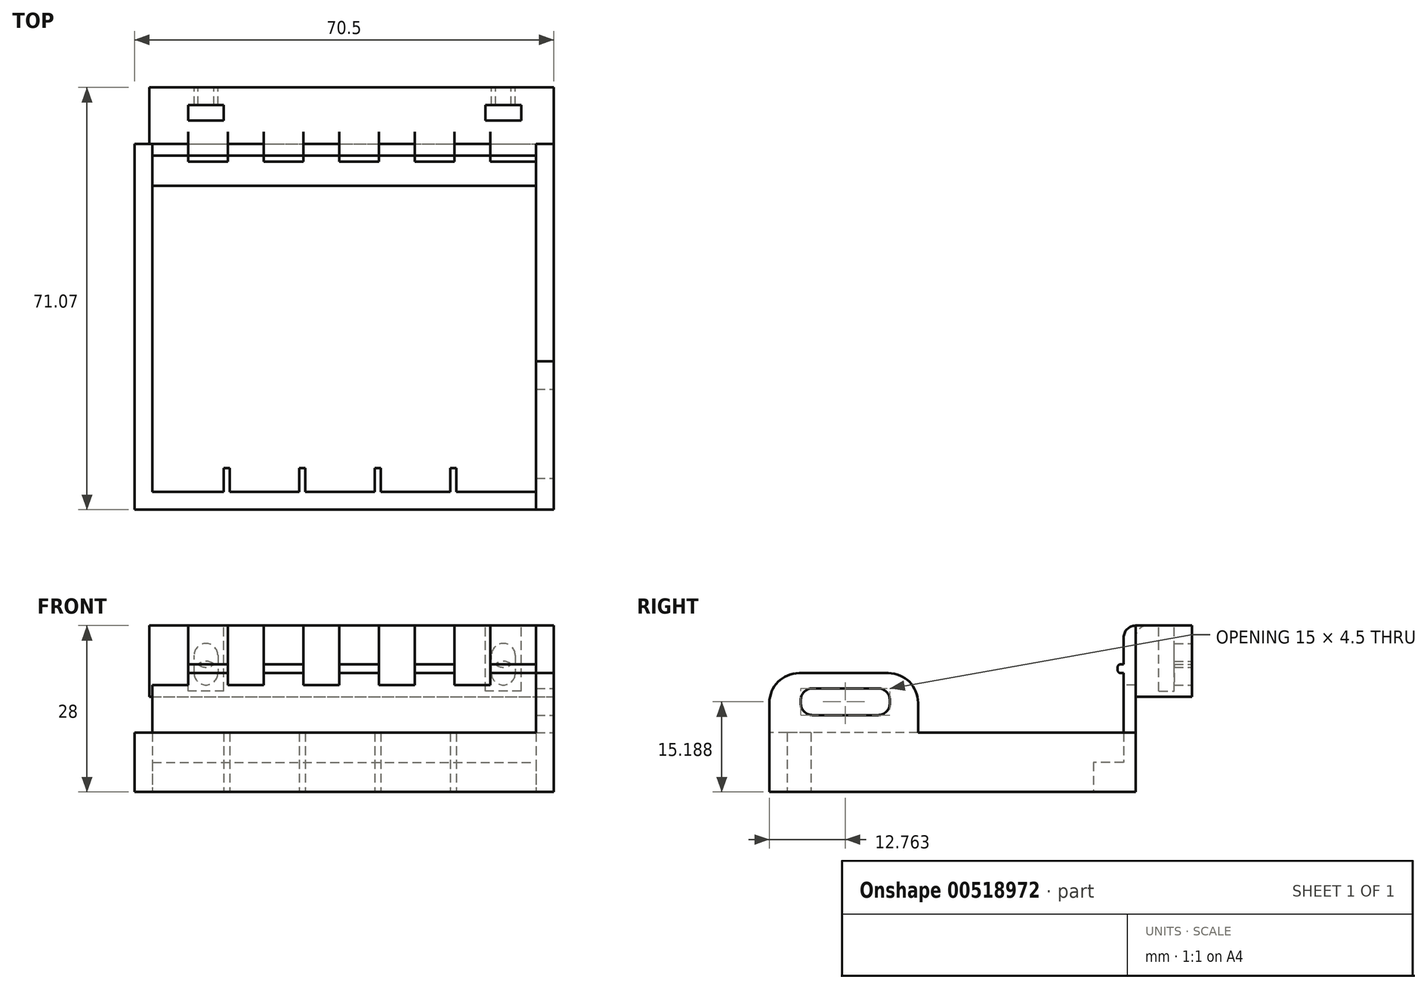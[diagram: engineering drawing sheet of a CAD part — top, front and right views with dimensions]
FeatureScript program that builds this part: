
annotation { "Feature Type Name" : "Feature", "Feature Type Description" : "" }
export const myFeature = defineFeature(function(context is Context, id is Id, definition is map)
    precondition{}
    {
        {
            var Q0;
            Q0=qCreatedBy(makeId("Top.planeOp"),FACE);
            var sketch = newSketch(context, id + "F0", { "sketchPlane" : qUnion([Q0])});
            skLineSegment(sketch, "E0.bottom", {"start": v(-11.89, 33.53) * mm, "end": v(52.61, 33.53) * mm});
            skLineSegment(sketch, "E0.top", {"start": v(-11.89, -23.04) * mm, "end": v(52.61, -23.04) * mm});
            skLineSegment(sketch, "E0.left", {"start": v(-11.89, 33.53) * mm, "end": v(-11.89, -23.04) * mm});
            skLineSegment(sketch, "E0.right", {"start": v(52.61, 33.53) * mm, "end": v(52.61, -23.04) * mm});
            skLineSegment(sketch, "E1.bottom", {"start": v(-14.89, 35.53) * mm, "end": v(55.61, 35.53) * mm});
            skLineSegment(sketch, "E1.top", {"start": v(-14.89, -26.04) * mm, "end": v(55.61, -26.04) * mm});
            skLineSegment(sketch, "E1.left", {"start": v(-14.89, 35.53) * mm, "end": v(-14.89, -26.04) * mm});
            skLineSegment(sketch, "E1.right", {"start": v(55.61, 35.53) * mm, "end": v(55.61, -26.04) * mm});
            skLineSegment(sketch, "E2", {"start": v(-11.89, -5.22) * mm, "end": v(-14.89, -5.22) * mm, "construction": true});
            skLineSegment(sketch, "E3", {"start": v(3.46, -23.04) * mm, "end": v(3.46, -26.04) * mm, "construction": true});
            skLineSegment(sketch, "E4", {"start": v(52.61, -8.08) * mm, "end": v(55.61, -8.08) * mm, "construction": true});
            skLineSegment(sketch, "E5.top", {"start": v(-11.89, 28.46) * mm, "end": v(52.61, 28.46) * mm});
            skLineSegment(sketch, "E5.left", {"start": v(-11.89, 33.53) * mm, "end": v(-11.89, 28.46) * mm});
            skLineSegment(sketch, "E5.right", {"start": v(52.61, 33.53) * mm, "end": v(52.61, 28.46) * mm});
            skLineSegment(sketch, "E6", {"start": v(0.11, -23.04) * mm, "end": v(0.11, -19.04) * mm});
            skLineSegment(sketch, "E7", {"start": v(0.11, -19.04) * mm, "end": v(1.11, -19.04) * mm});
            skLineSegment(sketch, "E8", {"start": v(1.11, -19.04) * mm, "end": v(1.11, -23.04) * mm});
            skLineSegment(sketch, "E9.bottom", {"start": v(12.81, -19.04) * mm, "end": v(13.81, -19.04) * mm});
            skLineSegment(sketch, "E9.top", {"start": v(12.81, -23.04) * mm, "end": v(13.81, -23.04) * mm});
            skLineSegment(sketch, "E9.left", {"start": v(12.81, -19.04) * mm, "end": v(12.81, -23.04) * mm});
            skLineSegment(sketch, "E9.right", {"start": v(13.81, -19.04) * mm, "end": v(13.81, -23.04) * mm});
            skLineSegment(sketch, "E10.bottom", {"start": v(25.51, -19.04) * mm, "end": v(26.51, -19.04) * mm});
            skLineSegment(sketch, "E10.top", {"start": v(25.51, -23.04) * mm, "end": v(26.51, -23.04) * mm});
            skLineSegment(sketch, "E10.left", {"start": v(25.51, -19.04) * mm, "end": v(25.51, -23.04) * mm});
            skLineSegment(sketch, "E10.right", {"start": v(26.51, -19.04) * mm, "end": v(26.51, -23.04) * mm});
            skLineSegment(sketch, "E11.bottom", {"start": v(38.21, -19.04) * mm, "end": v(39.21, -19.04) * mm});
            skLineSegment(sketch, "E11.top", {"start": v(38.21, -23.04) * mm, "end": v(39.21, -23.04) * mm});
            skLineSegment(sketch, "E11.left", {"start": v(38.21, -19.04) * mm, "end": v(38.21, -23.04) * mm});
            skLineSegment(sketch, "E11.right", {"start": v(39.21, -19.04) * mm, "end": v(39.21, -23.04) * mm});
            skSolve(sketch);
        }
        {
            var Q0;
            Q0=makeQuery(id+"F0.imprint","IMPRINT",FACE,{"disambiguationData":[TD([[makeQuery(id+"F0.imprint","IMPRINT",EDGE,{"derivedFrom":sQuery(id+"F0.wireOp",EDGE,"E0.top")}),-1.0]])]});
            var Q1;
            {var subQ0=sQuery(id+"F0.wireOp",EDGE,"E6");Q1=makeQuery(id+"F0.imprint","IMPRINT",FACE,{"disambiguationData":[TD([[makeQuery(id+"F0.imprint","IMPRINT",EDGE,{"derivedFrom":subQ0}),-1.0]])]});}
            var Q2;
            Q2=makeQuery(id+"F0.imprint","IMPRINT",FACE,{"disambiguationData":[TD([[makeQuery(id+"F0.imprint","IMPRINT",EDGE,{"derivedFrom":sQuery(id+"F0.wireOp",EDGE,"E9.bottom")}),-1.0]])]});
            var Q3;
            Q3=makeQuery(id+"F0.imprint","IMPRINT",FACE,{"disambiguationData":[TD([[makeQuery(id+"F0.imprint","IMPRINT",EDGE,{"derivedFrom":sQuery(id+"F0.wireOp",EDGE,"E10.bottom")}),-1.0]])]});
            var Q4;
            Q4=makeQuery(id+"F0.imprint","IMPRINT",FACE,{"disambiguationData":[TD([[makeQuery(id+"F0.imprint","IMPRINT",EDGE,{"derivedFrom":sQuery(id+"F0.wireOp",EDGE,"E11.bottom")}),-1.0]])]});
            extrude(context, id + "F1", {"entities" : qUnion([Q0, Q1, Q2, Q3, Q4]), "depth" : 10 * mm, "offsetDistance" : 25 * mm});
        }
        {
            var Q0;
            Q0=makeQuery(id+"F0.imprint","IMPRINT",FACE,{"disambiguationData":[TD([[makeQuery(id+"F0.imprint","IMPRINT",EDGE,{"derivedFrom":sQuery(id+"F0.wireOp",EDGE,"E0.bottom")}),-1.0]])]});
            extrude(context, id + "F2", {"entities" : qUnion([Q0]), "operationType" : NewBodyOperationType.ADD, "depth" : 5 * mm, "offsetDistance" : 25 * mm});
        }
        {
            var Q0;
            Q0=makeQuery(id+"F1.opExtrude","CAP_FACE",FACE,{"disambiguationData":[OSD([sQuery(id+"F0.wireOp",EDGE,"E0.top"),sQuery(id+"F0.wireOp",EDGE,"E0.left"),sQuery(id+"F0.wireOp",EDGE,"E0.right"),sQuery(id+"F0.wireOp",EDGE,"E1.bottom"),sQuery(id+"F0.wireOp",EDGE,"E1.top"),sQuery(id+"F0.wireOp",EDGE,"E1.left"),sQuery(id+"F0.wireOp",EDGE,"E1.right"),sQuery(id+"F0.wireOp",EDGE,"E0.bottom"),sQuery(id+"F0.wireOp",EDGE,"E5.left"),sQuery(id+"F0.wireOp",EDGE,"E5.right"),sQuery(id+"F0.wireOp",EDGE,"E6"),sQuery(id+"F0.wireOp",EDGE,"E7"),sQuery(id+"F0.wireOp",EDGE,"E8")])],"isStart":false});
            var sketch = newSketch(context, id + "F3", { "sketchPlane" : qUnion([Q0])});
            skLineSegment(sketch, "E12.bottom", {"start": v(-11.89, 33.53) * mm, "end": v(52.61, 33.53) * mm});
            skLineSegment(sketch, "E12.top", {"start": v(-11.89, 35.53) * mm, "end": v(52.61, 35.53) * mm});
            skLineSegment(sketch, "E12.left", {"start": v(-11.89, 33.53) * mm, "end": v(-11.89, 35.53) * mm});
            skLineSegment(sketch, "E12.right", {"start": v(52.61, 33.53) * mm, "end": v(52.61, 35.53) * mm});
            skSolve(sketch);
        }
        {
            var Q0;
            Q0=makeQuery(id+"F3.imprint","IMPRINT",FACE,{"disambiguationData":[TD([[makeQuery(id+"F3.imprint","IMPRINT",EDGE,{"derivedFrom":sQuery(id+"F3.wireOp",EDGE,"E12.bottom")}),1.0]])]});
            extrude(context, id + "F4", {"entities" : qUnion([Q0]), "operationType" : NewBodyOperationType.ADD, "depth" : 18 * mm, "offsetDistance" : 25 * mm});
        }
        {
            var Q0;
            Q0=makeQuery(id+"F4.opExtrude","SWEPT_FACE",FACE,{"disambiguationData":[OSD([sQuery(id+"F3.wireOp",EDGE,"E12.right")])]});
            var sketch = newSketch(context, id + "F5", { "sketchPlane" : qUnion([Q0])});
            skLineSegment(sketch, "E13.bottom", {"start": v(33.53, 21.5) * mm, "end": v(32.53, 21.5) * mm});
            skLineSegment(sketch, "E13.top", {"start": v(33.53, 20) * mm, "end": v(32.53, 20) * mm});
            skLineSegment(sketch, "E13.left", {"start": v(33.53, 21.5) * mm, "end": v(33.53, 20) * mm});
            skLineSegment(sketch, "E13.right", {"start": v(32.53, 21.5) * mm, "end": v(32.53, 20) * mm});
            skSolve(sketch);
        }
        {
            var Q0;
            Q0=makeQuery(id+"F5.imprint","IMPRINT",FACE,{"disambiguationData":[TD([[makeQuery(id+"F5.imprint","IMPRINT",EDGE,{"derivedFrom":sQuery(id+"F5.wireOp",EDGE,"E13.bottom")}),1.0]])]});
            extrude(context, id + "F6", {"entities" : qUnion([Q0]), "operationType" : NewBodyOperationType.ADD, "oppositeDirection" : true, "depth" : 64.5 * mm, "offsetDistance" : 25 * mm});
        }
        {
            var Q0;
            Q0=makeQuery(id+"F6.opExtrude","SWEPT_EDGE",EDGE,{"disambiguationData":[OSD([sQuery(id+"F5.wireOp",EDGE,"E13.bottom"),sQuery(id+"F5.wireOp",EDGE,"E13.right")])]});
            var Q1;
            Q1=makeQuery(id+"F6.opExtrude","SWEPT_EDGE",EDGE,{"disambiguationData":[OSD([sQuery(id+"F5.wireOp",EDGE,"E13.top"),sQuery(id+"F5.wireOp",EDGE,"E13.right")])]});
            fillet(context, id + "F7", {"entities" : qUnion([Q0, Q1]), "radius" : 0.5 * mm, "tangentPropagation" : true, "allowEdgeOverflow" : false});
        }
        {
            var Q0;
            Q0=makeQuery(id+"F4.opExtrude","CAP_FACE",FACE,{"disambiguationData":[OSD([sQuery(id+"F3.wireOp",EDGE,"E12.bottom"),sQuery(id+"F3.wireOp",EDGE,"E12.top"),sQuery(id+"F3.wireOp",EDGE,"E12.left"),sQuery(id+"F3.wireOp",EDGE,"E12.right")])],"isStart":false});
            var sketch = newSketch(context, id + "F8", { "sketchPlane" : qUnion([Q0])});
            skLineSegment(sketch, "E14.bottom", {"start": v(-11.89, 35.53) * mm, "end": v(-5.89, 35.53) * mm});
            skLineSegment(sketch, "E14.top", {"start": v(-11.89, 26.38) * mm, "end": v(-5.89, 26.38) * mm});
            skLineSegment(sketch, "E14.left", {"start": v(-11.89, 35.53) * mm, "end": v(-11.89, 26.38) * mm});
            skLineSegment(sketch, "E14.right", {"start": v(-5.89, 35.53) * mm, "end": v(-5.89, 26.38) * mm});
            skLineSegment(sketch, "E15.bottom", {"start": v(0.81, 35.53) * mm, "end": v(6.81, 35.53) * mm});
            skLineSegment(sketch, "E15.top", {"start": v(0.81, 26.38) * mm, "end": v(6.81, 26.38) * mm});
            skLineSegment(sketch, "E15.left", {"start": v(0.81, 35.53) * mm, "end": v(0.81, 26.38) * mm});
            skLineSegment(sketch, "E15.right", {"start": v(6.81, 35.53) * mm, "end": v(6.81, 26.38) * mm});
            skLineSegment(sketch, "E16.bottom", {"start": v(13.51, 35.53) * mm, "end": v(19.51, 35.53) * mm});
            skLineSegment(sketch, "E16.top", {"start": v(13.51, 26.38) * mm, "end": v(19.51, 26.38) * mm});
            skLineSegment(sketch, "E16.left", {"start": v(13.51, 35.53) * mm, "end": v(13.51, 26.38) * mm});
            skLineSegment(sketch, "E16.right", {"start": v(19.51, 35.53) * mm, "end": v(19.51, 26.38) * mm});
            skLineSegment(sketch, "E17.bottom", {"start": v(26.21, 35.53) * mm, "end": v(32.21, 35.53) * mm});
            skLineSegment(sketch, "E17.top", {"start": v(26.21, 26.38) * mm, "end": v(32.21, 26.38) * mm});
            skLineSegment(sketch, "E17.left", {"start": v(26.21, 35.53) * mm, "end": v(26.21, 26.38) * mm});
            skLineSegment(sketch, "E17.right", {"start": v(32.21, 35.53) * mm, "end": v(32.21, 26.38) * mm});
            skLineSegment(sketch, "E18.bottom", {"start": v(38.91, 35.53) * mm, "end": v(44.91, 35.53) * mm});
            skLineSegment(sketch, "E18.top", {"start": v(38.91, 26.38) * mm, "end": v(44.91, 26.38) * mm});
            skLineSegment(sketch, "E18.left", {"start": v(38.91, 35.53) * mm, "end": v(38.91, 26.38) * mm});
            skLineSegment(sketch, "E18.right", {"start": v(44.91, 35.53) * mm, "end": v(44.91, 26.38) * mm});
            skLineSegment(sketch, "E19", {"start": v(-11.89, 30.96) * mm, "end": v(0.81, 30.96) * mm, "construction": true});
            skLineSegment(sketch, "E20", {"start": v(0.81, 30.96) * mm, "end": v(13.51, 30.96) * mm, "construction": true});
            skLineSegment(sketch, "E21", {"start": v(13.51, 30.96) * mm, "end": v(26.21, 30.96) * mm, "construction": true});
            skLineSegment(sketch, "E22", {"start": v(26.21, 30.96) * mm, "end": v(38.91, 30.96) * mm, "construction": true});
            skSolve(sketch);
        }
        {
            var Q0;
            Q0=qSketchRegion(id+"F8",true);
            extrude(context, id + "F9", {"entities" : qUnion([Q0]), "operationType" : NewBodyOperationType.REMOVE, "oppositeDirection" : true, "depth" : 10 * mm, "offsetDistance" : 25 * mm});
        }
        {
            var Q0;
            Q0=makeQuery(id+"F1.opExtrude","SWEPT_FACE",FACE,{"disambiguationData":[OSD([sQuery(id+"F0.wireOp",EDGE,"E1.right")])]});
            var sketch = newSketch(context, id + "F10", { "sketchPlane" : qUnion([Q0])});
            skLineSegment(sketch, "E23.bottom", {"start": v(35.53, 28) * mm, "end": v(45.03, 28) * mm});
            skLineSegment(sketch, "E23.top", {"start": v(35.53, 16) * mm, "end": v(45.03, 16) * mm});
            skLineSegment(sketch, "E23.left", {"start": v(35.53, 28) * mm, "end": v(35.53, 16) * mm});
            skLineSegment(sketch, "E23.right", {"start": v(45.03, 28) * mm, "end": v(45.03, 16) * mm});
            skSolve(sketch);
        }
        {
            var Q0;
            Q0=makeQuery(id+"F10.imprint","IMPRINT",FACE,{"disambiguationData":[TD([[makeQuery(id+"F10.imprint","IMPRINT",EDGE,{"derivedFrom":sQuery(id+"F10.wireOp",EDGE,"E23.bottom")}),-1.0]])]});
            extrude(context, id + "F11", {"entities" : qUnion([Q0]), "operationType" : NewBodyOperationType.ADD, "oppositeDirection" : true, "depth" : 68 * mm, "offsetDistance" : 25 * mm});
        }
        {
            var Q0;
            Q0=makeQuery(id+"F11.opExtrude","SWEPT_FACE",FACE,{"disambiguationData":[OSD([sQuery(id+"F10.wireOp",EDGE,"E23.right")])]});
            var sketch = newSketch(context, id + "F12", { "sketchPlane" : qUnion([Q0])});
            skCircle(sketch, "E24", {"center": v(-47.11, 20) * mm, "radius": 2 * mm});
            skCircle(sketch, "E25", {"center": v(2.89, 20) * mm, "radius": 2 * mm});
            skCircle(sketch, "E26", {"center": v(-47.11, 23) * mm, "radius": 2 * mm});
            skCircle(sketch, "E27", {"center": v(2.89, 23) * mm, "radius": 2 * mm});
            skLineSegment(sketch, "E28", {"start": v(2.89, 23) * mm, "end": v(0.89, 23) * mm, "construction": true});
            skLineSegment(sketch, "E29", {"start": v(0.89, 23) * mm, "end": v(0.89, 20) * mm});
            skLineSegment(sketch, "E30", {"start": v(0.89, 20) * mm, "end": v(4.89, 20) * mm, "construction": true});
            skLineSegment(sketch, "E31", {"start": v(4.89, 20) * mm, "end": v(4.89, 23) * mm});
            skLineSegment(sketch, "E32", {"start": v(-47.11, 23) * mm, "end": v(-49.11, 23) * mm, "construction": true});
            skLineSegment(sketch, "E33", {"start": v(-49.11, 23) * mm, "end": v(-49.11, 20) * mm});
            skLineSegment(sketch, "E34", {"start": v(-49.11, 20) * mm, "end": v(-45.11, 20) * mm, "construction": true});
            skLineSegment(sketch, "E35", {"start": v(-45.11, 20) * mm, "end": v(-45.11, 23) * mm});
            skSolve(sketch);
        }
        {
            var Q0;
            Q0 = qSketchRegion(id + "F12", true);
            var Q1;
            {var subQ0=sQuery(id+"F12.wireOp",EDGE,"E26");var subQ1=sQuery(id+"F12.wireOp",EDGE,"E24");var subQ2=makeQuery(id+"F12.imprint","INTERSECT",VERTEX,{"disambiguationData":[OD(0.0)],"derivedFrom":[subQ1,subQ0]});Q1=makeQuery(id+"F12.imprint","IMPRINT",FACE,{"disambiguationData":[TD([[makeQuery(id+"F12.imprint","IMPRINT",EDGE,{"disambiguationData":[TD([[subQ2,-1.0]])],"derivedFrom":subQ1}),1.0]])]});}
            var Q2;
            {var subQ0=sQuery(id+"F12.wireOp",EDGE,"E27");var subQ1=sQuery(id+"F12.wireOp",EDGE,"E25");var subQ2=makeQuery(id+"F12.imprint","INTERSECT",VERTEX,{"disambiguationData":[OD(0.0)],"derivedFrom":[subQ1,subQ0]});Q2=makeQuery(id+"F12.imprint","IMPRINT",FACE,{"disambiguationData":[TD([[makeQuery(id+"F12.imprint","IMPRINT",EDGE,{"disambiguationData":[TD([[subQ2,-1.0]])],"derivedFrom":subQ1}),1.0]])]});}
            extrude(context, id + "F13", {"entities" : qUnion([Q0, Q1, Q2]), "operationType" : NewBodyOperationType.REMOVE, "oppositeDirection" : true, "depth" : 4 * mm, "offsetDistance" : 25 * mm});
        }
        {
            var Q0;
            {var subQ0=sQuery(id+"F3.wireOp",EDGE,"E12.bottom");var subQ3=sQuery(id+"F3.wireOp",EDGE,"E12.top");var subQ6=sQuery(id+"F3.wireOp",EDGE,"E12.right");var subQ7=makeQuery(id+"F4.opExtrude","CAP_FACE",FACE,{"disambiguationData":[OSD([subQ0,subQ3,sQuery(id+"F3.wireOp",EDGE,"E12.left"),subQ6])],"isStart":false});Q0=makeQuery(id+"F11.boolean.opBoolean","MERGE",FACE,{"derivedFrom":[makeQuery(id+"F9.boolean.opBoolean","SPLIT",FACE,{"disambiguationData":[TD([makeQuery(id+"F4.opExtrude","SWEPT_FACE",FACE,{"disambiguationData":[OSD([subQ6])]})])],"derivedFrom":subQ7}),makeQuery(id+"F9.boolean.opBoolean","SPLIT",FACE,{"disambiguationData":[TD([makeQuery(id+"F9.opExtrude","SWEPT_FACE",FACE,{"disambiguationData":[OSD([sQuery(id+"F8.wireOp",EDGE,"E14.right")])]})])],"derivedFrom":subQ7}),makeQuery(id+"F9.boolean.opBoolean","SPLIT",FACE,{"disambiguationData":[TD([makeQuery(id+"F9.opExtrude","SWEPT_FACE",FACE,{"disambiguationData":[OSD([sQuery(id+"F8.wireOp",EDGE,"E15.right")])]})])],"derivedFrom":subQ7}),makeQuery(id+"F9.boolean.opBoolean","SPLIT",FACE,{"disambiguationData":[TD([makeQuery(id+"F9.opExtrude","SWEPT_FACE",FACE,{"disambiguationData":[OSD([sQuery(id+"F8.wireOp",EDGE,"E16.right")])]})])],"derivedFrom":subQ7}),makeQuery(id+"F9.boolean.opBoolean","SPLIT",FACE,{"disambiguationData":[TD([makeQuery(id+"F9.opExtrude","SWEPT_FACE",FACE,{"disambiguationData":[OSD([sQuery(id+"F8.wireOp",EDGE,"E17.right")])]})])],"derivedFrom":subQ7}),makeQuery(id+"F11.opExtrude","SWEPT_FACE",FACE,{"disambiguationData":[OSD([sQuery(id+"F10.wireOp",EDGE,"E23.bottom")])]})]});}
            var sketch = newSketch(context, id + "F14", { "sketchPlane" : qUnion([Q0])});
            skLineSegment(sketch, "E36.bottom", {"start": v(0.11, 39.43) * mm, "end": v(-5.89, 39.43) * mm});
            skLineSegment(sketch, "E36.top", {"start": v(0.11, 42.03) * mm, "end": v(-5.89, 42.03) * mm});
            skLineSegment(sketch, "E36.left", {"start": v(0.11, 39.43) * mm, "end": v(0.11, 42.03) * mm});
            skLineSegment(sketch, "E36.right", {"start": v(-5.89, 39.43) * mm, "end": v(-5.89, 42.03) * mm});
            skPoint(sketch, "E36.middle", {"position": v(-2.89, 40.73) * mm});
            skLineSegment(sketch, "E37.bottom", {"start": v(50.11, 39.43) * mm, "end": v(44.11, 39.43) * mm});
            skLineSegment(sketch, "E37.top", {"start": v(50.11, 42.03) * mm, "end": v(44.11, 42.03) * mm});
            skLineSegment(sketch, "E37.left", {"start": v(50.11, 39.43) * mm, "end": v(50.11, 42.03) * mm});
            skLineSegment(sketch, "E37.right", {"start": v(44.11, 39.43) * mm, "end": v(44.11, 42.03) * mm});
            skPoint(sketch, "E37.middle", {"position": v(47.11, 40.73) * mm});
            skSolve(sketch);
        }
        {
            var Q0;
            Q0 = qSketchRegion(id + "F14", true);
            extrude(context, id + "F15", {"entities" : qUnion([Q0]), "operationType" : NewBodyOperationType.REMOVE, "oppositeDirection" : true, "depth" : 11 * mm, "offsetDistance" : 25 * mm});
        }
        {
            var Q0;
            Q0=makeQuery(id+"F1.opExtrude","CAP_FACE",FACE,{"disambiguationData":[OSD([sQuery(id+"F0.wireOp",EDGE,"E0.top"),sQuery(id+"F0.wireOp",EDGE,"E0.left"),sQuery(id+"F0.wireOp",EDGE,"E0.right"),sQuery(id+"F0.wireOp",EDGE,"E1.bottom"),sQuery(id+"F0.wireOp",EDGE,"E1.top"),sQuery(id+"F0.wireOp",EDGE,"E1.left"),sQuery(id+"F0.wireOp",EDGE,"E1.right"),sQuery(id+"F0.wireOp",EDGE,"E0.bottom"),sQuery(id+"F0.wireOp",EDGE,"E5.left"),sQuery(id+"F0.wireOp",EDGE,"E5.right"),sQuery(id+"F0.wireOp",EDGE,"E6"),sQuery(id+"F0.wireOp",EDGE,"E7"),sQuery(id+"F0.wireOp",EDGE,"E8"),sQuery(id+"F0.wireOp",EDGE,"E9.bottom"),sQuery(id+"F0.wireOp",EDGE,"E9.left"),sQuery(id+"F0.wireOp",EDGE,"E9.right"),sQuery(id+"F0.wireOp",EDGE,"E10.bottom"),sQuery(id+"F0.wireOp",EDGE,"E10.left"),sQuery(id+"F0.wireOp",EDGE,"E10.right"),sQuery(id+"F0.wireOp",EDGE,"E11.bottom"),sQuery(id+"F0.wireOp",EDGE,"E11.left"),sQuery(id+"F0.wireOp",EDGE,"E11.right")])],"isStart":false});
            var sketch = newSketch(context, id + "F16", { "sketchPlane" : qUnion([Q0])});
            skLineSegment(sketch, "E38.bottom", {"start": v(55.61, -26.04) * mm, "end": v(52.61, -26.04) * mm});
            skLineSegment(sketch, "E38.top", {"start": v(55.61, -1.04) * mm, "end": v(52.61, -1.04) * mm});
            skLineSegment(sketch, "E38.left", {"start": v(55.61, -26.04) * mm, "end": v(55.61, -1.04) * mm});
            skLineSegment(sketch, "E38.right", {"start": v(52.61, -26.04) * mm, "end": v(52.61, -1.04) * mm});
            skSolve(sketch);
        }
        {
            var Q0;
            {var subQ4=sQuery(id+"F16.wireOp",EDGE,"E38.bottom");Q0=makeQuery(id+"F16.imprint","IMPRINT",FACE,{"disambiguationData":[TD([[makeQuery(id+"F16.imprint","IMPRINT",EDGE,{"derivedFrom":subQ4}),1.0]])]});}
            extrude(context, id + "F17", {"entities" : qUnion([Q0]), "operationType" : NewBodyOperationType.ADD, "depth" : 10 * mm, "offsetDistance" : 25 * mm});
        }
        {
            var Q0;
            Q0=makeQuery(id+"F17.boolean.opBoolean","MERGE",FACE,{"derivedFrom":[makeQuery(id+"F1.opExtrude","SWEPT_FACE",FACE,{"disambiguationData":[OSD([sQuery(id+"F0.wireOp",EDGE,"E1.right")])]}),makeQuery(id+"F17.opExtrude","SWEPT_FACE",FACE,{"disambiguationData":[OSD([sQuery(id+"F16.wireOp",EDGE,"E38.left")])]})]});
            var sketch = newSketch(context, id + "F18", { "sketchPlane" : qUnion([Q0])});
            skLineSegment(sketch, "E39.bottom", {"start": v(-20.78, 17.44) * mm, "end": v(-5.78, 17.44) * mm});
            skLineSegment(sketch, "E39.top", {"start": v(-20.78, 12.94) * mm, "end": v(-5.78, 12.94) * mm});
            skLineSegment(sketch, "E39.left", {"start": v(-20.78, 17.44) * mm, "end": v(-20.78, 12.94) * mm});
            skLineSegment(sketch, "E39.right", {"start": v(-5.78, 17.44) * mm, "end": v(-5.78, 12.94) * mm});
            skSolve(sketch);
        }
        {
            var Q0;
            Q0=makeQuery(id+"F18.imprint","IMPRINT",FACE,{"disambiguationData":[TD([[makeQuery(id+"F18.imprint","IMPRINT",EDGE,{"derivedFrom":sQuery(id+"F18.wireOp",EDGE,"E39.bottom")}),-1.0]])]});
            extrude(context, id + "F19", {"entities" : qUnion([Q0]), "operationType" : NewBodyOperationType.REMOVE, "oppositeDirection" : true, "depth" : 25 * mm, "offsetDistance" : 25 * mm});
        }
        {
            var Q0;
            Q0=makeQuery(id+"F17.opExtrude","CAP_EDGE",EDGE,{"disambiguationData":[OSD([sQuery(id+"F16.wireOp",EDGE,"E38.top")])],"isStart":false});
            var Q1;
            Q1=makeQuery(id+"F17.opExtrude","CAP_EDGE",EDGE,{"disambiguationData":[OSD([sQuery(id+"F16.wireOp",EDGE,"E38.bottom")])],"isStart":false});
            fillet(context, id + "F20", {"entities" : qUnion([Q0, Q1]), "radius" : 5 * mm, "tangentPropagation" : true, "allowEdgeOverflow" : false});
        }
        {
            var Q0;
            Q0=makeQuery(id+"F19.boolean.opBoolean","COPY",EDGE,{"derivedFrom":makeQuery(id+"F19.opExtrude","SWEPT_EDGE",EDGE,{"disambiguationData":[OSD([sQuery(id+"F18.wireOp",EDGE,"E39.bottom"),sQuery(id+"F18.wireOp",EDGE,"E39.left")])]})});
            var Q1;
            Q1=makeQuery(id+"F19.boolean.opBoolean","COPY",EDGE,{"derivedFrom":makeQuery(id+"F19.opExtrude","SWEPT_EDGE",EDGE,{"disambiguationData":[OSD([sQuery(id+"F18.wireOp",EDGE,"E39.top"),sQuery(id+"F18.wireOp",EDGE,"E39.left")])]})});
            var Q2;
            Q2=makeQuery(id+"F19.boolean.opBoolean","COPY",EDGE,{"derivedFrom":makeQuery(id+"F19.opExtrude","SWEPT_EDGE",EDGE,{"disambiguationData":[OSD([sQuery(id+"F18.wireOp",EDGE,"E39.top"),sQuery(id+"F18.wireOp",EDGE,"E39.right")])]})});
            var Q3;
            Q3=makeQuery(id+"F19.boolean.opBoolean","COPY",EDGE,{"derivedFrom":makeQuery(id+"F19.opExtrude","SWEPT_EDGE",EDGE,{"disambiguationData":[OSD([sQuery(id+"F18.wireOp",EDGE,"E39.bottom"),sQuery(id+"F18.wireOp",EDGE,"E39.right")])]})});
            var Q4;
            {var subQ0=sQuery(id+"F10.wireOp",EDGE,"E23.bottom");var subQ1=sQuery(id+"F10.wireOp",EDGE,"E23.left");Q4=makeQuery(id+"F11.boolean.opBoolean","SPLIT",EDGE,{"disambiguationData":[TD([makeQuery(id+"F9.boolean.opBoolean","COPY",FACE,{"derivedFrom":makeQuery(id+"F9.opExtrude","SWEPT_FACE",FACE,{"disambiguationData":[OSD([sQuery(id+"F8.wireOp",EDGE,"E18.left")])]})})])],"derivedFrom":makeQuery(id+"F11.opExtrude","SWEPT_EDGE",EDGE,{"disambiguationData":[OSD([subQ0,subQ1])]})});}
            var Q5;
            {var subQ0=sQuery(id+"F3.wireOp",EDGE,"E12.right");var subQ1=sQuery(id+"F3.wireOp",EDGE,"E12.bottom");Q5=makeQuery(id+"F9.boolean.opBoolean","SPLIT",EDGE,{"disambiguationData":[TD([makeQuery(id+"F4.opExtrude","SWEPT_FACE",FACE,{"disambiguationData":[OSD([subQ0])]})])],"derivedFrom":makeQuery(id+"F4.opExtrude","CAP_EDGE",EDGE,{"disambiguationData":[OSD([subQ1])],"isStart":false})});}
            var Q6;
            {var subQ0=sQuery(id+"F3.wireOp",EDGE,"E12.bottom");Q6=makeQuery(id+"F9.boolean.opBoolean","SPLIT",EDGE,{"disambiguationData":[TD([makeQuery(id+"F9.opExtrude","SWEPT_FACE",FACE,{"disambiguationData":[OSD([sQuery(id+"F8.wireOp",EDGE,"E17.right")])]})])],"derivedFrom":makeQuery(id+"F4.opExtrude","CAP_EDGE",EDGE,{"disambiguationData":[OSD([subQ0])],"isStart":false})});}
            var Q7;
            {var subQ0=sQuery(id+"F10.wireOp",EDGE,"E23.bottom");var subQ1=sQuery(id+"F10.wireOp",EDGE,"E23.left");Q7=makeQuery(id+"F11.boolean.opBoolean","SPLIT",EDGE,{"disambiguationData":[TD([makeQuery(id+"F9.boolean.opBoolean","COPY",FACE,{"derivedFrom":makeQuery(id+"F9.opExtrude","SWEPT_FACE",FACE,{"disambiguationData":[OSD([sQuery(id+"F8.wireOp",EDGE,"E17.left")])]})})])],"derivedFrom":makeQuery(id+"F11.opExtrude","SWEPT_EDGE",EDGE,{"disambiguationData":[OSD([subQ0,subQ1])]})});}
            var Q8;
            {var subQ0=sQuery(id+"F3.wireOp",EDGE,"E12.bottom");Q8=makeQuery(id+"F9.boolean.opBoolean","SPLIT",EDGE,{"disambiguationData":[TD([makeQuery(id+"F9.opExtrude","SWEPT_FACE",FACE,{"disambiguationData":[OSD([sQuery(id+"F8.wireOp",EDGE,"E16.right")])]})])],"derivedFrom":makeQuery(id+"F4.opExtrude","CAP_EDGE",EDGE,{"disambiguationData":[OSD([subQ0])],"isStart":false})});}
            var Q9;
            {var subQ0=sQuery(id+"F10.wireOp",EDGE,"E23.bottom");var subQ1=sQuery(id+"F10.wireOp",EDGE,"E23.left");Q9=makeQuery(id+"F11.boolean.opBoolean","SPLIT",EDGE,{"disambiguationData":[TD([makeQuery(id+"F9.boolean.opBoolean","COPY",FACE,{"derivedFrom":makeQuery(id+"F9.opExtrude","SWEPT_FACE",FACE,{"disambiguationData":[OSD([sQuery(id+"F8.wireOp",EDGE,"E16.left")])]})})])],"derivedFrom":makeQuery(id+"F11.opExtrude","SWEPT_EDGE",EDGE,{"disambiguationData":[OSD([subQ0,subQ1])]})});}
            var Q10;
            {var subQ0=sQuery(id+"F3.wireOp",EDGE,"E12.bottom");Q10=makeQuery(id+"F9.boolean.opBoolean","SPLIT",EDGE,{"disambiguationData":[TD([makeQuery(id+"F9.opExtrude","SWEPT_FACE",FACE,{"disambiguationData":[OSD([sQuery(id+"F8.wireOp",EDGE,"E15.right")])]})])],"derivedFrom":makeQuery(id+"F4.opExtrude","CAP_EDGE",EDGE,{"disambiguationData":[OSD([subQ0])],"isStart":false})});}
            var Q11;
            {var subQ0=sQuery(id+"F10.wireOp",EDGE,"E23.bottom");var subQ1=sQuery(id+"F10.wireOp",EDGE,"E23.left");Q11=makeQuery(id+"F11.boolean.opBoolean","SPLIT",EDGE,{"disambiguationData":[TD([makeQuery(id+"F9.boolean.opBoolean","COPY",FACE,{"derivedFrom":makeQuery(id+"F9.opExtrude","SWEPT_FACE",FACE,{"disambiguationData":[OSD([sQuery(id+"F8.wireOp",EDGE,"E15.left")])]})})])],"derivedFrom":makeQuery(id+"F11.opExtrude","SWEPT_EDGE",EDGE,{"disambiguationData":[OSD([subQ0,subQ1])]})});}
            var Q12;
            {var subQ0=sQuery(id+"F3.wireOp",EDGE,"E12.bottom");Q12=makeQuery(id+"F9.boolean.opBoolean","SPLIT",EDGE,{"disambiguationData":[TD([makeQuery(id+"F9.opExtrude","SWEPT_FACE",FACE,{"disambiguationData":[OSD([sQuery(id+"F8.wireOp",EDGE,"E14.right")])]})])],"derivedFrom":makeQuery(id+"F4.opExtrude","CAP_EDGE",EDGE,{"disambiguationData":[OSD([subQ0])],"isStart":false})});}
            var Q13;
            {var subQ0=sQuery(id+"F10.wireOp",EDGE,"E23.left");var subQ1=sQuery(id+"F10.wireOp",EDGE,"E23.bottom");Q13=makeQuery(id+"F11.boolean.opBoolean","SPLIT",EDGE,{"disambiguationData":[TD([makeQuery(id+"F9.boolean.opBoolean","COPY",FACE,{"derivedFrom":makeQuery(id+"F9.opExtrude","SWEPT_FACE",FACE,{"disambiguationData":[OSD([sQuery(id+"F8.wireOp",EDGE,"E14.right")])]})})])],"derivedFrom":makeQuery(id+"F11.opExtrude","SWEPT_EDGE",EDGE,{"disambiguationData":[OSD([subQ1,subQ0])]})});}
            fillet(context, id + "F21", {"entities" : qUnion([Q0, Q1, Q2, Q3, Q4, Q5, Q6, Q7, Q8, Q9, Q10, Q11, Q12, Q13]), "radius" : 2 * mm, "tangentPropagation" : true, "allowEdgeOverflow" : false});
        }
    });
